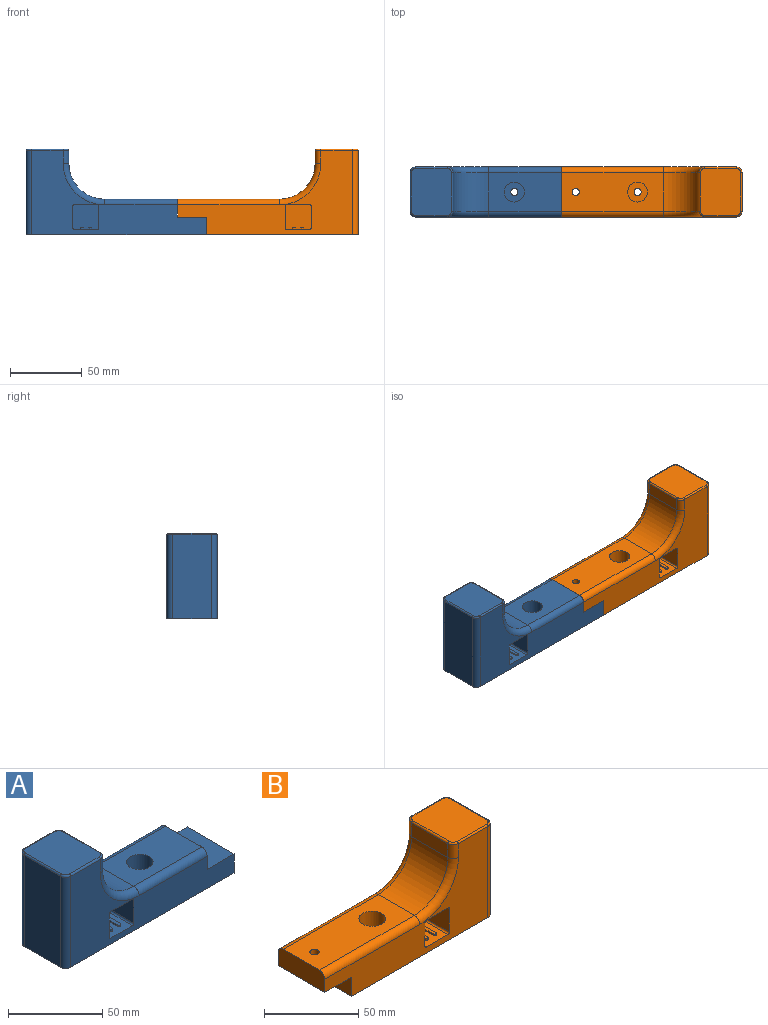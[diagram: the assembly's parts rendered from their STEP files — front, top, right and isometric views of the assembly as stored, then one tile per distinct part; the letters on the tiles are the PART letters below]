
ASSEMBLY  parts=2 mates=1
PART A: 48 faces, bbox 126.3x35.7x60 mm
  f0: plane 50.9x27mm, normal (0,0,1), area 1220.4mm2, adj f2,f3,f11,f13,f45
  f1: plane 122x59mm, normal (0,-1,0), area 3095.2mm2, adj f3,f5,f8,f14,f15,f16,f17,f18
  f2: cylinder r=4mm len=50.9mm, axis (1,0,0), area 319.8mm2, adj f0,f6,f24,f45
  f3: cylinder r=4mm len=50.9mm, axis (-1,0,0), area 319.8mm2, adj f0,f1,f26,f45
  f4: cylinder r=2.5mm len=5mm, axis (0,0,-1), area 78.5mm2, adj f8,f12
  f5: plane 35x12.49mm, normal (1,0,0), area 437.2mm2, adj f1,f6,f8,f46
  f6: plane 122x59mm, normal (0,1,0), area 3407.4mm2, adj f2,f5,f8,f23,f24,f27,f29,f45
  f7: plane 59x27mm, normal (-1,0,0), area 1593mm2, adj f8,f27,f28,f33
  f8: plane 126x35mm, normal (0,0,-1), area 4363.9mm2, adj f1,f4,f5,f6,f7,f27,f28,f47
  f9: plane 27x9mm, normal (1,0,0), area 243mm2, adj f13,f23,f25,f32
  f10: plane 33x28mm, normal (0,0,1), area 916.3mm2, adj f29,f30,f31,f32,f33,f34,f35,f36
  f11: cylinder r=7mm len=20mm, axis (0,0,1), area 879.6mm2, adj f0,f12
  f12: plane 14x14mm, normal (0,0,1), area 134.3mm2, adj f4,f11
  f13: cylinder r=25mm len=27mm, axis (0,-1,0), area 1060.3mm2, adj f0,f9,f24,f26
  f14: plane 17x16.2mm, normal (0,0,1), area 224.3mm2, adj f1,f15,f21,f22,f37,f38,f39,f41
  f15: cylinder r=1mm len=17mm, axis (0,-1,0), area 26.7mm2, adj f1,f14,f16,f22
  f16: plane 17x15.2mm, normal (-1,0,0), area 258.4mm2, adj f1,f15,f17,f22
  f17: cylinder r=1mm len=17mm, axis (0,-1,0), area 26.7mm2, adj f1,f16,f18,f22
  f18: plane 17x16.2mm, normal (0,0,-1), area 275.4mm2, adj f1,f17,f19,f22
  f19: cylinder r=1mm len=17mm, axis (0,-1,0), area 26.7mm2, adj f1,f18,f20,f22
  f20: plane 17x15.2mm, normal (1,0,0), area 258.4mm2, adj f1,f19,f21,f22
  f21: cylinder r=1mm len=17mm, axis (0,-1,0), area 26.7mm2, adj f1,f14,f20,f22
  f22: plane 18.2x17.2mm, normal (0,-1,0), area 308.2mm2, adj f14,f15,f16,f17,f18,f19,f20,f21
  f23: cylinder r=4mm len=9mm, axis (0,0,1), area 56.5mm2, adj f6,f9,f24,f30
  f24: torus R=29mm, axis (0,-1,0), area 261.1mm2, adj f2,f6,f13,f23
  f25: cylinder r=4mm len=9mm, axis (0,0,-1), area 56.5mm2, adj f1,f9,f26,f34
  f26: torus R=29mm, axis (0,-1,0), area 261.1mm2, adj f1,f3,f13,f25
  f27: cylinder r=4mm len=59mm, axis (0,0,-1), area 370.7mm2, adj f6,f7,f8,f31
  f28: cylinder r=4mm len=59mm, axis (0,0,1), area 370.7mm2, adj f1,f7,f8,f35
  f29: cylinder r=1mm len=22mm, axis (1,0,0), area 34.6mm2, adj f6,f10,f30,f31
  f30: torus R=3mm, axis (0,0,1), area 9mm2, adj f10,f23,f29,f32
  f31: torus R=3mm, axis (0,0,1), area 9mm2, adj f10,f27,f29,f33
  f32: cylinder r=1mm len=27mm, axis (0,-1,0), area 42.4mm2, adj f9,f10,f30,f34
  f33: cylinder r=1mm len=27mm, axis (0,1,0), area 42.4mm2, adj f7,f10,f31,f35
  f34: torus R=3mm, axis (0,0,1), area 9mm2, adj f10,f25,f32,f36
  f35: torus R=3mm, axis (0,0,1), area 9mm2, adj f10,f28,f33,f36
  f36: cylinder r=1mm len=22mm, axis (-1,0,0), area 34.6mm2, adj f1,f10,f34,f35
  f37: plane 12x1mm, normal (-1,0,0), area 12mm2, adj f14,f22,f38,f40
  f38: cylinder r=1mm len=2mm, axis (0,0,-1), area 3.1mm2, adj f14,f37,f39,f40
  f39: plane 12x1mm, normal (1,0,0), area 12mm2, adj f14,f22,f38,f40
  f40: plane 13x2mm, normal (0,0,1), area 25.6mm2, adj f22,f37,f38,f39
  f41: plane 12x1mm, normal (1,0,0), area 12mm2, adj f14,f22,f43,f44
  f42: plane 12x1mm, normal (-1,0,0), area 12mm2, adj f14,f22,f43,f44
  f43: cylinder r=1mm len=2mm, axis (0,0,-1), area 3.1mm2, adj f14,f41,f42,f44
  f44: plane 13x2mm, normal (0,0,1), area 25.6mm2, adj f22,f41,f42,f43
  f45: plane 35x12.51mm, normal (1,0,0), area 431mm2, adj f0,f1,f2,f3,f6,f46
  f46: plane 35x20.1mm, normal (0,0,1), area 683.9mm2, adj f1,f5,f6,f45,f47
  f47: cylinder r=2.5mm len=12.49mm, axis (0,0,1), area 196.2mm2, adj f8,f46
PART B: 48 faces, bbox 126.3x35.7x60 mm
  f0: plane 17x16.2mm, normal (0,0,1), area 224.3mm2, adj f1,f18,f19,f20,f37,f38,f39,f41
  f1: plane 122x59mm, normal (0,-1,0), area 3017.3mm2, adj f0,f3,f7,f13,f14,f15,f16,f17
  f2: cylinder r=2.5mm len=5mm, axis (0,0,-1), area 78.5mm2, adj f7,f11
  f3: plane 35x12.49mm, normal (-1,0,0), area 430.3mm2, adj f1,f5,f6,f21,f24,f46
  f4: plane 59x27mm, normal (1,0,0), area 1593mm2, adj f7,f27,f28,f33
  f5: plane 122x59mm, normal (0,1,0), area 3329.5mm2, adj f3,f7,f24,f25,f26,f28,f29,f45
  f6: plane 71x27mm, normal (0,0,1), area 1743.4mm2, adj f3,f10,f12,f21,f24,f47
  f7: plane 106.1x35mm, normal (0,0,-1), area 3687mm2, adj f1,f2,f4,f5,f27,f28,f45
  f8: plane 27x9mm, normal (-1,0,0), area 243mm2, adj f12,f23,f26,f32
  f9: plane 33x28mm, normal (0,0,1), area 916.3mm2, adj f29,f30,f31,f32,f33,f34,f35,f36
  f10: cylinder r=7mm len=20mm, axis (0,0,1), area 879.6mm2, adj f6,f11
  f11: plane 14x14mm, normal (0,0,1), area 134.3mm2, adj f2,f10
  f12: cylinder r=25mm len=27mm, axis (0,1,0), area 1060.3mm2, adj f6,f8,f22,f25
  f13: plane 17x15.2mm, normal (-1,0,0), area 258.4mm2, adj f1,f14,f19,f20
  f14: cylinder r=1mm len=17mm, axis (0,-1,0), area 26.7mm2, adj f1,f13,f15,f20
  f15: plane 17x16.2mm, normal (0,0,-1), area 275.4mm2, adj f1,f14,f16,f20
  f16: cylinder r=1mm len=17mm, axis (0,-1,0), area 26.7mm2, adj f1,f15,f17,f20
  f17: plane 17x15.2mm, normal (1,0,0), area 258.4mm2, adj f1,f16,f18,f20
  f18: cylinder r=1mm len=17mm, axis (0,-1,0), area 26.7mm2, adj f0,f1,f17,f20
  f19: cylinder r=1mm len=17mm, axis (0,-1,0), area 26.7mm2, adj f0,f1,f13,f20
  f20: plane 18.2x17.2mm, normal (0,-1,0), area 308.2mm2, adj f0,f13,f14,f15,f16,f17,f18,f19
  f21: cylinder r=4mm len=71mm, axis (-1,0,0), area 446.1mm2, adj f1,f3,f6,f22
  f22: torus R=29mm, axis (0,1,0), area 261.1mm2, adj f1,f12,f21,f23
  f23: cylinder r=4mm len=9mm, axis (0,0,1), area 56.5mm2, adj f1,f8,f22,f34
  f24: cylinder r=4mm len=71mm, axis (1,0,0), area 446.1mm2, adj f3,f5,f6,f25
  f25: torus R=29mm, axis (0,1,0), area 261.1mm2, adj f5,f12,f24,f26
  f26: cylinder r=4mm len=9mm, axis (0,0,-1), area 56.5mm2, adj f5,f8,f25,f30
  f27: cylinder r=4mm len=59mm, axis (0,0,-1), area 370.7mm2, adj f1,f4,f7,f35
  f28: cylinder r=4mm len=59mm, axis (0,0,1), area 370.7mm2, adj f4,f5,f7,f31
  f29: cylinder r=1mm len=22mm, axis (1,0,0), area 34.6mm2, adj f5,f9,f30,f31
  f30: torus R=3mm, axis (0,0,1), area 9mm2, adj f9,f26,f29,f32
  f31: torus R=3mm, axis (0,0,1), area 9mm2, adj f9,f28,f29,f33
  f32: cylinder r=1mm len=27mm, axis (0,1,0), area 42.4mm2, adj f8,f9,f30,f34
  f33: cylinder r=1mm len=27mm, axis (0,-1,0), area 42.4mm2, adj f4,f9,f31,f35
  f34: torus R=3mm, axis (0,0,1), area 9mm2, adj f9,f23,f32,f36
  f35: torus R=3mm, axis (0,0,1), area 9mm2, adj f9,f27,f33,f36
  f36: cylinder r=1mm len=22mm, axis (-1,0,0), area 34.6mm2, adj f1,f9,f34,f35
  f37: plane 12x1mm, normal (1,0,0), area 12mm2, adj f0,f20,f39,f40
  f38: plane 12x1mm, normal (-1,0,0), area 12mm2, adj f0,f20,f39,f40
  f39: cylinder r=1mm len=2mm, axis (0,0,-1), area 3.1mm2, adj f0,f37,f38,f40
  f40: plane 13x2mm, normal (0,0,1), area 25.6mm2, adj f20,f37,f38,f39
  f41: plane 12x1mm, normal (-1,0,0), area 12mm2, adj f0,f20,f42,f44
  f42: cylinder r=1mm len=2mm, axis (0,0,-1), area 3.1mm2, adj f0,f41,f43,f44
  f43: plane 12x1mm, normal (1,0,0), area 12mm2, adj f0,f20,f42,f44
  f44: plane 13x2mm, normal (0,0,1), area 25.6mm2, adj f20,f41,f42,f43
  f45: plane 35x12.51mm, normal (-1,0,0), area 437.9mm2, adj f1,f5,f7,f46
  f46: plane 35x19.9mm, normal (0,0,-1), area 676.9mm2, adj f1,f3,f5,f45,f47
  f47: cylinder r=2.5mm len=12.49mm, axis (0,0,-1), area 196.2mm2, adj f6,f46
PLACE A t=(-3.1,0,0.02)mm
PLACE B t=(99,0,0)mm
MATE fastened A.f47 <-> B.f47  axis (0,0,1) through (52.85,0,12.51)mm
